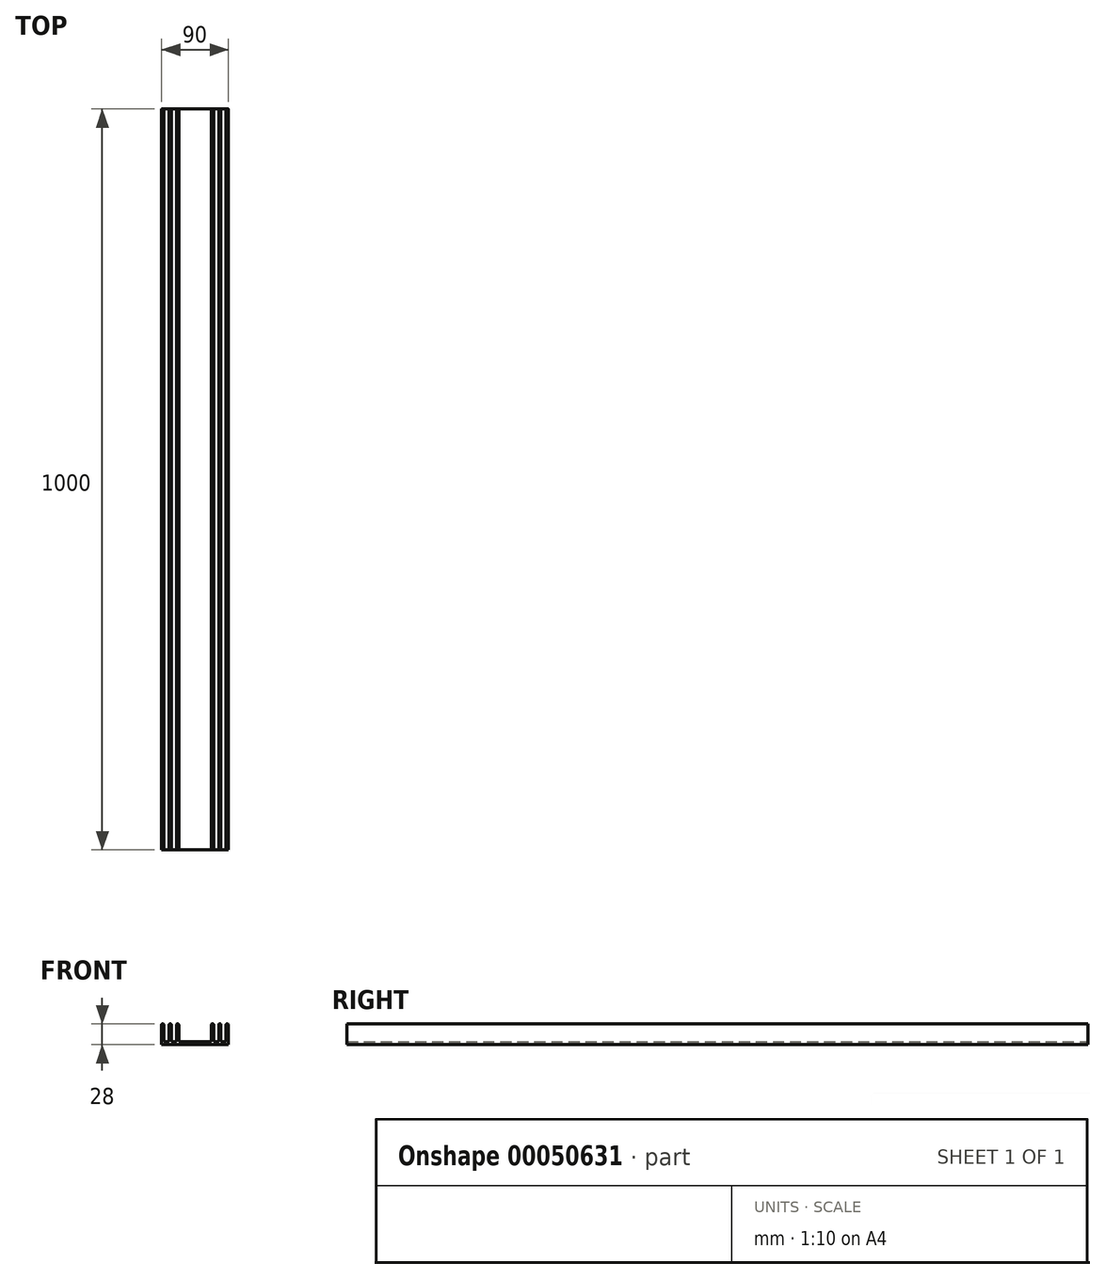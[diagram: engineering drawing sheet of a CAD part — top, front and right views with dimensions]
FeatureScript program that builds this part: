
annotation { "Feature Type Name" : "Feature", "Feature Type Description" : "" }
export const myFeature = defineFeature(function(context is Context, id is Id, definition is map)
    precondition{}
    {
        {
            var Q0;
            Q0=qCreatedBy(makeId("Front.planeOp"),FACE);
            var sketch = newSketch(context, id + "F0", { "sketchPlane" : qUnion([Q0])});
            skLineSegment(sketch, "E0", {"start": v(0, 0) * mm, "end": v(45, 0) * mm});
            skLineSegment(sketch, "E1", {"start": v(45, 0) * mm, "end": v(45, 4) * mm});
            skLineSegment(sketch, "E2", {"start": v(42, 4) * mm, "end": v(35, 4) * mm});
            skLineSegment(sketch, "E3", {"start": v(45, 4) * mm, "end": v(45, 27) * mm});
            skLineSegment(sketch, "E4", {"start": v(42, 27) * mm, "end": v(42, 4) * mm});
            skLineSegment(sketch, "E5", {"start": v(43, 28) * mm, "end": v(44, 28) * mm});
            skPoint(sketch, "E6.visualSharp", {"position": v(42, 28) * mm});
            skArc(sketch, "E6.filletArc", {"start": v(43, 28) * mm, "mid": v(42.3, 27.7) * mm, "end": v(42, 27) * mm});
            skPoint(sketch, "E7.visualSharp", {"position": v(45, 28) * mm});
            skArc(sketch, "E7.filletArc", {"start": v(45, 27) * mm, "mid": v(44.7, 27.7) * mm, "end": v(44, 28) * mm});
            skPoint(sketch, "E8.1.0.0", {"position": v(35, 28) * mm});
            skLineSegment(sketch, "E8.1.0.1", {"start": v(32, 27) * mm, "end": v(32, 4) * mm});
            skPoint(sketch, "E8.1.0.2", {"position": v(32, 28) * mm});
            skLineSegment(sketch, "E8.1.0.3", {"start": v(35, 4) * mm, "end": v(35, 27) * mm});
            skArc(sketch, "E8.1.0.4", {"start": v(35, 27) * mm, "mid": v(34.7, 27.7) * mm, "end": v(34, 28) * mm});
            skArc(sketch, "E8.1.0.5", {"start": v(33, 28) * mm, "mid": v(32.3, 27.7) * mm, "end": v(32, 27) * mm});
            skLineSegment(sketch, "E8.1.0.6", {"start": v(33, 28) * mm, "end": v(34, 28) * mm});
            skPoint(sketch, "E8.2.0.0", {"position": v(25, 28) * mm});
            skLineSegment(sketch, "E8.2.0.1", {"start": v(22, 27) * mm, "end": v(22, 4) * mm});
            skPoint(sketch, "E8.2.0.2", {"position": v(22, 28) * mm});
            skLineSegment(sketch, "E8.2.0.3", {"start": v(25, 4) * mm, "end": v(25, 27) * mm});
            skArc(sketch, "E8.2.0.4", {"start": v(25, 27) * mm, "mid": v(24.7, 27.7) * mm, "end": v(24, 28) * mm});
            skArc(sketch, "E8.2.0.5", {"start": v(23, 28) * mm, "mid": v(22.3, 27.7) * mm, "end": v(22, 27) * mm});
            skLineSegment(sketch, "E8.2.0.6", {"start": v(23, 28) * mm, "end": v(24, 28) * mm});
            skLineSegment(sketch, "E8.direction1", {"start": v(45, 28) * mm, "end": v(35, 28) * mm, "construction": true});
            skLineSegment(sketch, "E9.trimOffspring", {"start": v(22, 4) * mm, "end": v(0, 4) * mm});
            skLineSegment(sketch, "E10.trimOffspring", {"start": v(32, 4) * mm, "end": v(25, 4) * mm});
            skLineSegment(sketch, "E11", {"start": v(0, 0) * mm, "end": v(0, 4) * mm});
            skSolve(sketch);
        }
        {
            var Q0;
            Q0=qSketchRegion(id+"F0",true);
            extrude(context, id + "F1", {"entities" : qUnion([Q0]), "depth" : 1000 * mm});
        }
        {
            var Q0;
            Q0=makeQuery(id+"F1.opExtrude","SWEPT_BODY",BODY,{"disambiguationData":[OSD([sQuery(id+"F0.wireOp",EDGE,"E0"),sQuery(id+"F0.wireOp",EDGE,"E1"),sQuery(id+"F0.wireOp",EDGE,"E2"),sQuery(id+"F0.wireOp",EDGE,"E3"),sQuery(id+"F0.wireOp",EDGE,"E4"),sQuery(id+"F0.wireOp",EDGE,"E5"),sQuery(id+"F0.wireOp",EDGE,"E6.filletArc"),sQuery(id+"F0.wireOp",EDGE,"E7.filletArc"),sQuery(id+"F0.wireOp",EDGE,"E8.1.0.1"),sQuery(id+"F0.wireOp",EDGE,"E8.1.0.3"),sQuery(id+"F0.wireOp",EDGE,"E8.1.0.4"),sQuery(id+"F0.wireOp",EDGE,"E8.1.0.5"),sQuery(id+"F0.wireOp",EDGE,"E8.1.0.6"),sQuery(id+"F0.wireOp",EDGE,"E8.2.0.1"),sQuery(id+"F0.wireOp",EDGE,"E8.2.0.3"),sQuery(id+"F0.wireOp",EDGE,"E8.2.0.4"),sQuery(id+"F0.wireOp",EDGE,"E8.2.0.5"),sQuery(id+"F0.wireOp",EDGE,"E8.2.0.6"),sQuery(id+"F0.wireOp",EDGE,"E9.trimOffspring"),sQuery(id+"F0.wireOp",EDGE,"E10.trimOffspring"),sQuery(id+"F0.wireOp",EDGE,"E11")])]});
            var Q1;
            Q1=qCreatedBy(makeId("Right.planeOp"),FACE);
            mirror(context, id + "F2", {"operationType" : NewBodyOperationType.ADD, "entities" : qUnion([Q0]), "mirrorPlane" : qUnion([Q1])});
        }
    });
